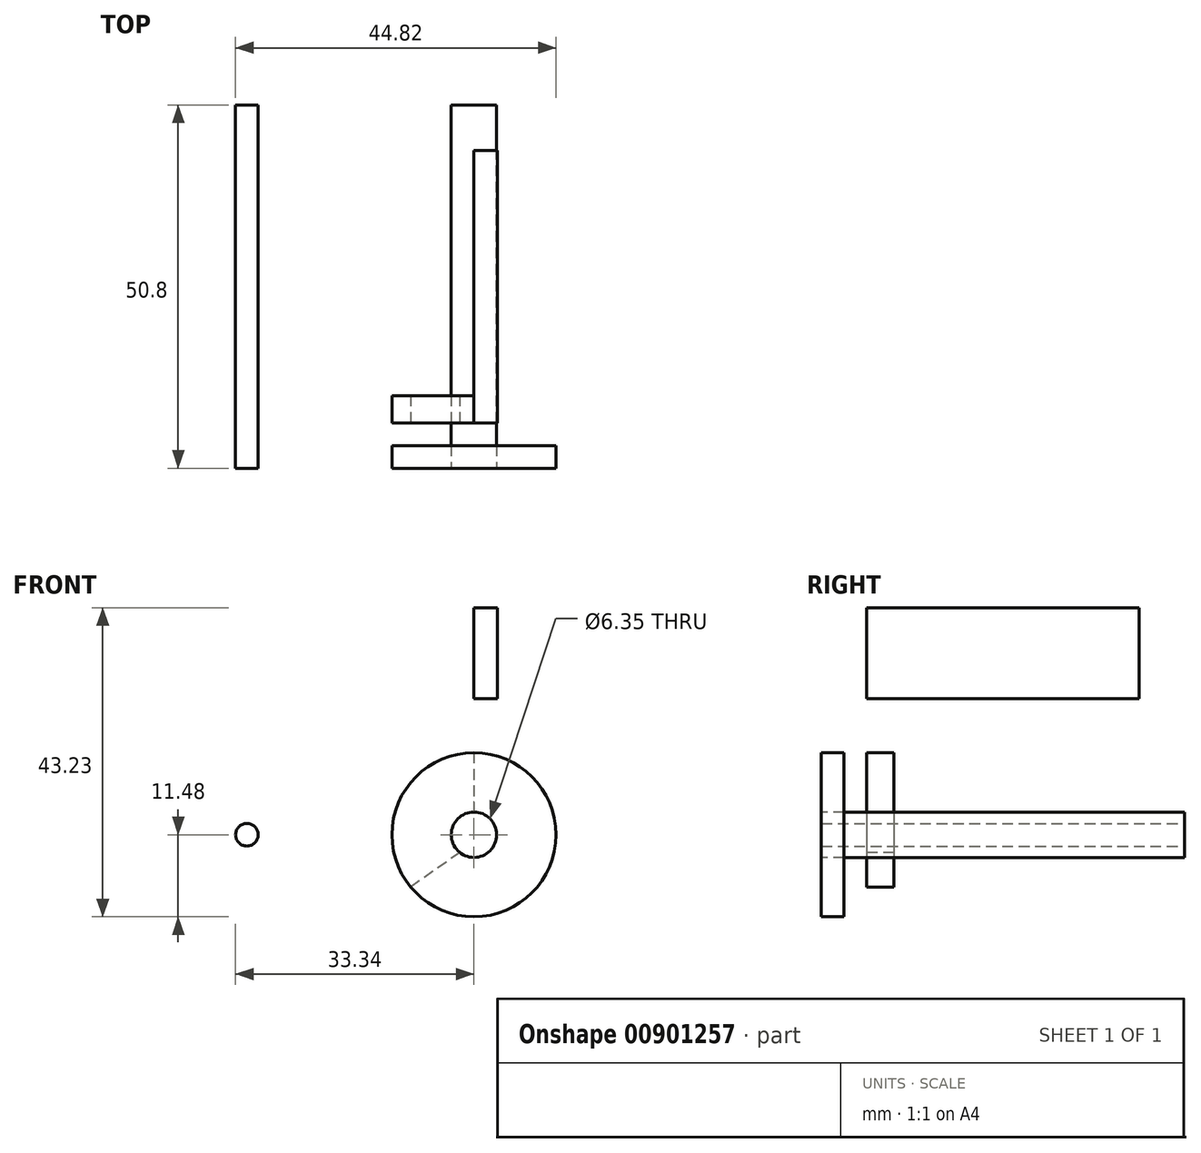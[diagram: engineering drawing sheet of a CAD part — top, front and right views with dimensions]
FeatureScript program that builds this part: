
annotation { "Feature Type Name" : "Feature", "Feature Type Description" : "" }
export const myFeature = defineFeature(function(context is Context, id is Id, definition is map)
    precondition{}
    {
        {
            var Q0;
            Q0=qCreatedBy(makeId("Front.planeOp"),FACE);
            var sketch = newSketch(context, id + "F0", { "sketchPlane" : qUnion([Q0])});
            skCircle(sketch, "E0", {"center": v(0, 0) * mm, "radius": 31.75 * mm});
            skCircle(sketch, "E1", {"center": v(0, 0) * mm, "radius": 3.18 * mm});
            skCircle(sketch, "E2", {"center": v(0, 0) * mm, "radius": 3.24 * mm});
            skLineSegment(sketch, "E3.bottom", {"start": v(0, 31.75) * mm, "end": v(3.25, 31.75) * mm});
            skLineSegment(sketch, "E3.top", {"start": v(0, 19.05) * mm, "end": v(3.25, 19.05) * mm});
            skLineSegment(sketch, "E3.left", {"start": v(0, 31.75) * mm, "end": v(0, 19.05) * mm});
            skLineSegment(sketch, "E3.right", {"start": v(3.25, 31.75) * mm, "end": v(3.25, 19.05) * mm});
            skCircle(sketch, "E4", {"center": v(-31.75, 0) * mm, "radius": 1.59 * mm});
            skSolve(sketch);
        }
        {
            var Q0;
            Q0=makeQuery(id+"F0.imprint","IMPRINT",FACE,{"disambiguationData":[TD([[makeQuery(id+"F0.imprint","IMPRINT",EDGE,{"derivedFrom":sQuery(id+"F0.wireOp",EDGE,"E1")}),1.0]])]});
            var Q1;
            {var subQ0=sQuery(id+"F0.wireOp",EDGE,"E4");var subQ1=sQuery(id+"F0.wireOp",EDGE,"E0");var subQ2=makeQuery(id+"F0.imprint","INTERSECT",VERTEX,{"disambiguationData":[OD(0.0)],"derivedFrom":[subQ1,subQ0]});Q1=makeQuery(id+"F0.imprint","IMPRINT",FACE,{"disambiguationData":[TD([[makeQuery(id+"F0.imprint","IMPRINT",EDGE,{"disambiguationData":[TD([[subQ2,-1.0]])],"derivedFrom":subQ1}),-1.0]])]});}
            var Q2;
            {var subQ0=sQuery(id+"F0.wireOp",EDGE,"E4");var subQ1=sQuery(id+"F0.wireOp",EDGE,"E0");var subQ2=makeQuery(id+"F0.imprint","INTERSECT",VERTEX,{"disambiguationData":[OD(0.0)],"derivedFrom":[subQ1,subQ0]});Q2=makeQuery(id+"F0.imprint","IMPRINT",FACE,{"disambiguationData":[TD([[makeQuery(id+"F0.imprint","IMPRINT",EDGE,{"disambiguationData":[TD([[subQ2,-1.0]])],"derivedFrom":subQ1}),1.0]])]});}
            extrude(context, id + "F1", {"entities" : qUnion([Q0, Q1, Q2]), "endBound" : BoundingType.SYMMETRIC, "depth" : 50.8 * mm, "offsetDistance" : 25.4 * mm});
        }
        {
            var Q0;
            {var subQ0=sQuery(id+"F0.wireOp",EDGE,"E3.bottom");Q0=makeQuery(id+"F0.imprint","IMPRINT",FACE,{"disambiguationData":[TD([[makeQuery(id+"F0.imprint","IMPRINT",EDGE,{"derivedFrom":subQ0}),-1.0]])]});}
            var Q1;
            {var subQ4=sQuery(id+"F0.wireOp",EDGE,"E3.top");Q1=makeQuery(id+"F0.imprint","IMPRINT",FACE,{"disambiguationData":[TD([[makeQuery(id+"F0.imprint","IMPRINT",EDGE,{"derivedFrom":subQ4}),1.0]])]});}
            extrude(context, id + "F2", {"entities" : qUnion([Q0, Q1]), "endBound" : BoundingType.SYMMETRIC, "depth" : 38.1 * mm, "offsetDistance" : 25.4 * mm});
        }
        {
            var Q0;
            Q0=makeQuery(id+"F2.opExtrude","CAP_FACE",FACE,{"disambiguationData":[OSD([sQuery(id+"F0.wireOp",EDGE,"E3.bottom"),sQuery(id+"F0.wireOp",EDGE,"E3.top"),sQuery(id+"F0.wireOp",EDGE,"E3.left"),sQuery(id+"F0.wireOp",EDGE,"E3.right")])],"isStart":false});
            var sketch = newSketch(context, id + "F3", { "sketchPlane" : qUnion([Q0])});
            skLineSegment(sketch, "E5.0.0", {"start": v(3.25, 19.05) * mm, "end": v(3.25, 31.75) * mm});
            skLineSegment(sketch, "E5.0.1", {"start": v(3.25, 31.75) * mm, "end": v(0, 31.75) * mm});
            skLineSegment(sketch, "E5.0.2", {"start": v(0, 31.75) * mm, "end": v(0, 19.05) * mm});
            skLineSegment(sketch, "E5.0.3", {"start": v(0, 19.05) * mm, "end": v(3.25, 19.05) * mm});
            skCircle(sketch, "E6.0.0", {"center": v(0, 0) * mm, "radius": 3.18 * mm});
            skArc(sketch, "E7.0.0", {"start": v(-31.71, 1.59) * mm, "mid": v(-30.16, 0) * mm, "end": v(-31.71, -1.59) * mm});
            skArc(sketch, "E7.0.1", {"start": v(-31.71, -1.59) * mm, "mid": v(21.85, -23.03) * mm, "end": v(3.25, 31.58) * mm});
            skLineSegment(sketch, "E7.0.2", {"start": v(3.25, 31.58) * mm, "end": v(3.25, 19.05) * mm});
            skLineSegment(sketch, "E7.0.3", {"start": v(3.25, 19.05) * mm, "end": v(0, 19.05) * mm});
            skLineSegment(sketch, "E7.0.4", {"start": v(0, 19.05) * mm, "end": v(0, 31.75) * mm});
            skArc(sketch, "E7.0.5", {"start": v(0, 31.75) * mm, "mid": v(-21.88, 23) * mm, "end": v(-31.71, 1.59) * mm});
            skLineSegment(sketch, "E8", {"start": v(0, 19.05) * mm, "end": v(0, 3.18) * mm});
            skLineSegment(sketch, "E9", {"start": v(-1.97, -2.5) * mm, "end": v(-25.47, -18.95) * mm});
            skArc(sketch, "E10", {"start": v(0, 11.48) * mm, "mid": v(-10.38, 4.89) * mm, "end": v(-8.85, -7.31) * mm});
            skSolve(sketch);
        }
        {
            var Q0;
            {var subQ0=sQuery(id+"F3.wireOp",EDGE,"E7.0.2");Q0=makeQuery(id+"F3.imprint","IMPRINT",FACE,{"disambiguationData":[TD([[makeQuery(id+"F3.imprint","IMPRINT",EDGE,{"derivedFrom":subQ0}),1.0]])]});}
            var Q1;
            {var subQ5=sQuery(id+"F3.wireOp",EDGE,"E10");Q1=makeQuery(id+"F3.imprint","IMPRINT",FACE,{"disambiguationData":[TD([[makeQuery(id+"F3.imprint","IMPRINT",EDGE,{"derivedFrom":subQ5}),1.0]])]});}
            extrude(context, id + "F4", {"entities" : qUnion([Q0, Q1]), "oppositeDirection" : true, "depth" : 3.8 * mm, "offsetDistance" : 25.4 * mm});
        }
        {
            var Q0;
            Q0=makeQuery(id+"F1.opExtrude","CAP_FACE",FACE,{"disambiguationData":[OSD([sQuery(id+"F0.wireOp",EDGE,"E4")])],"isStart":false});
            var sketch = newSketch(context, id + "F5", { "sketchPlane" : qUnion([Q0])});
            skLineSegment(sketch, "E11.0.0", {"start": v(-25.47, -18.95) * mm, "end": v(-8.85, -7.31) * mm});
            skArc(sketch, "E11.0.1", {"start": v(-8.85, -7.31) * mm, "mid": v(-10.38, 4.89) * mm, "end": v(0, 11.48) * mm});
            skLineSegment(sketch, "E11.0.2", {"start": v(0, 11.48) * mm, "end": v(0, 19.05) * mm});
            skLineSegment(sketch, "E11.0.3", {"start": v(0, 19.05) * mm, "end": v(0, 31.75) * mm});
            skLineSegment(sketch, "E12.0.0", {"start": v(0, 11.48) * mm, "end": v(0, 3.18) * mm});
            skArc(sketch, "E12.0.1", {"start": v(0, 3.18) * mm, "mid": v(3, -1.04) * mm, "end": v(-1.97, -2.5) * mm});
            skLineSegment(sketch, "E12.0.2", {"start": v(-1.97, -2.5) * mm, "end": v(-8.85, -7.31) * mm});
            skLineSegment(sketch, "E12.0.3", {"start": v(-8.85, -7.31) * mm, "end": v(-25.47, -18.95) * mm});
            skArc(sketch, "E12.0.4", {"start": v(-25.47, -18.95) * mm, "mid": v(27.6, -15.69) * mm, "end": v(3.25, 31.58) * mm});
            skLineSegment(sketch, "E12.0.5", {"start": v(3.25, 31.58) * mm, "end": v(3.25, 19.05) * mm});
            skLineSegment(sketch, "E12.0.6", {"start": v(3.25, 19.05) * mm, "end": v(0, 19.05) * mm});
            skLineSegment(sketch, "E12.0.7", {"start": v(0, 19.05) * mm, "end": v(0, 11.48) * mm});
            skCircle(sketch, "E13.0", {"center": v(0, 0) * mm, "radius": 3.18 * mm});
            skLineSegment(sketch, "E14", {"start": v(0, 0) * mm, "end": v(31.75, 0) * mm});
            skPoint(sketch, "E14.endSnap0", {"position": v(3.18, 0) * mm});
            skLineSegment(sketch, "E15", {"start": v(0, 0) * mm, "end": v(-31.74, 0) * mm});
            skArc(sketch, "E16.0", {"start": v(0, 31.75) * mm, "mid": v(-21.88, 23) * mm, "end": v(-31.71, 1.59) * mm});
            skArc(sketch, "E17.0", {"start": v(-31.71, -1.59) * mm, "mid": v(21.85, -23.03) * mm, "end": v(3.25, 31.58) * mm});
            skCircle(sketch, "E18", {"center": v(0, 0) * mm, "radius": 11.48 * mm});
            skSolve(sketch);
        }
        {
            var Q0;
            {var subQ1=sQuery(id+"F5.wireOp",EDGE,"E12.0.3");Q0=makeQuery(id+"F5.imprint","IMPRINT",FACE,{"disambiguationData":[TD([[makeQuery(id+"F5.imprint","IMPRINT",EDGE,{"derivedFrom":subQ1}),-1.0]])]});}
            var Q1;
            {var subQ0=sQuery(id+"F5.wireOp",EDGE,"E12.0.2");Q1=makeQuery(id+"F5.imprint","IMPRINT",FACE,{"disambiguationData":[TD([[makeQuery(id+"F5.imprint","IMPRINT",EDGE,{"derivedFrom":subQ0}),-1.0]])]});}
            var Q2;
            {var subQ1=sQuery(id+"F5.wireOp",EDGE,"E12.0.2");Q2=makeQuery(id+"F5.imprint","IMPRINT",FACE,{"disambiguationData":[TD([[makeQuery(id+"F5.imprint","IMPRINT",EDGE,{"derivedFrom":subQ1}),1.0]])]});}
            var Q3;
            {var subQ0=sQuery(id+"F5.wireOp",EDGE,"E12.0.0");Q3=makeQuery(id+"F5.imprint","IMPRINT",FACE,{"disambiguationData":[TD([[makeQuery(id+"F5.imprint","IMPRINT",EDGE,{"derivedFrom":subQ0}),-1.0]])]});}
            var Q4;
            {var subQ0=sQuery(id+"F5.wireOp",EDGE,"E12.0.0");Q4=makeQuery(id+"F5.imprint","IMPRINT",FACE,{"disambiguationData":[TD([[makeQuery(id+"F5.imprint","IMPRINT",EDGE,{"derivedFrom":subQ0}),1.0]])]});}
            var Q5;
            {var subQ0=sQuery(id+"F5.wireOp",EDGE,"E12.0.3");Q5=makeQuery(id+"F5.imprint","IMPRINT",FACE,{"disambiguationData":[TD([[makeQuery(id+"F5.imprint","IMPRINT",EDGE,{"derivedFrom":subQ0}),1.0]])]});}
            var Q6;
            Q6=makeQuery(id+"F4.opExtrude","CAP_FACE",FACE,{"disambiguationData":[OSD([sQuery(id+"F3.wireOp",EDGE,"E6.0.0"),sQuery(id+"F3.wireOp",EDGE,"E7.0.1"),sQuery(id+"F3.wireOp",EDGE,"E7.0.2"),sQuery(id+"F3.wireOp",EDGE,"E7.0.3"),sQuery(id+"F3.wireOp",EDGE,"E8"),sQuery(id+"F3.wireOp",EDGE,"E9"),sQuery(id+"F3.wireOp",EDGE,"E10")])],"isStart":true});
            extrude(context, id + "F6", {"entities" : qUnion([Q0, Q1, Q2, Q3, Q4, Q5]), "oppositeDirection" : true, "depth" : 3.17 * mm, "endBoundEntityFace" : qUnion([Q6]), "hasOffset" : true, "offsetDistance" : 1.27 * mm});
        }
    });
